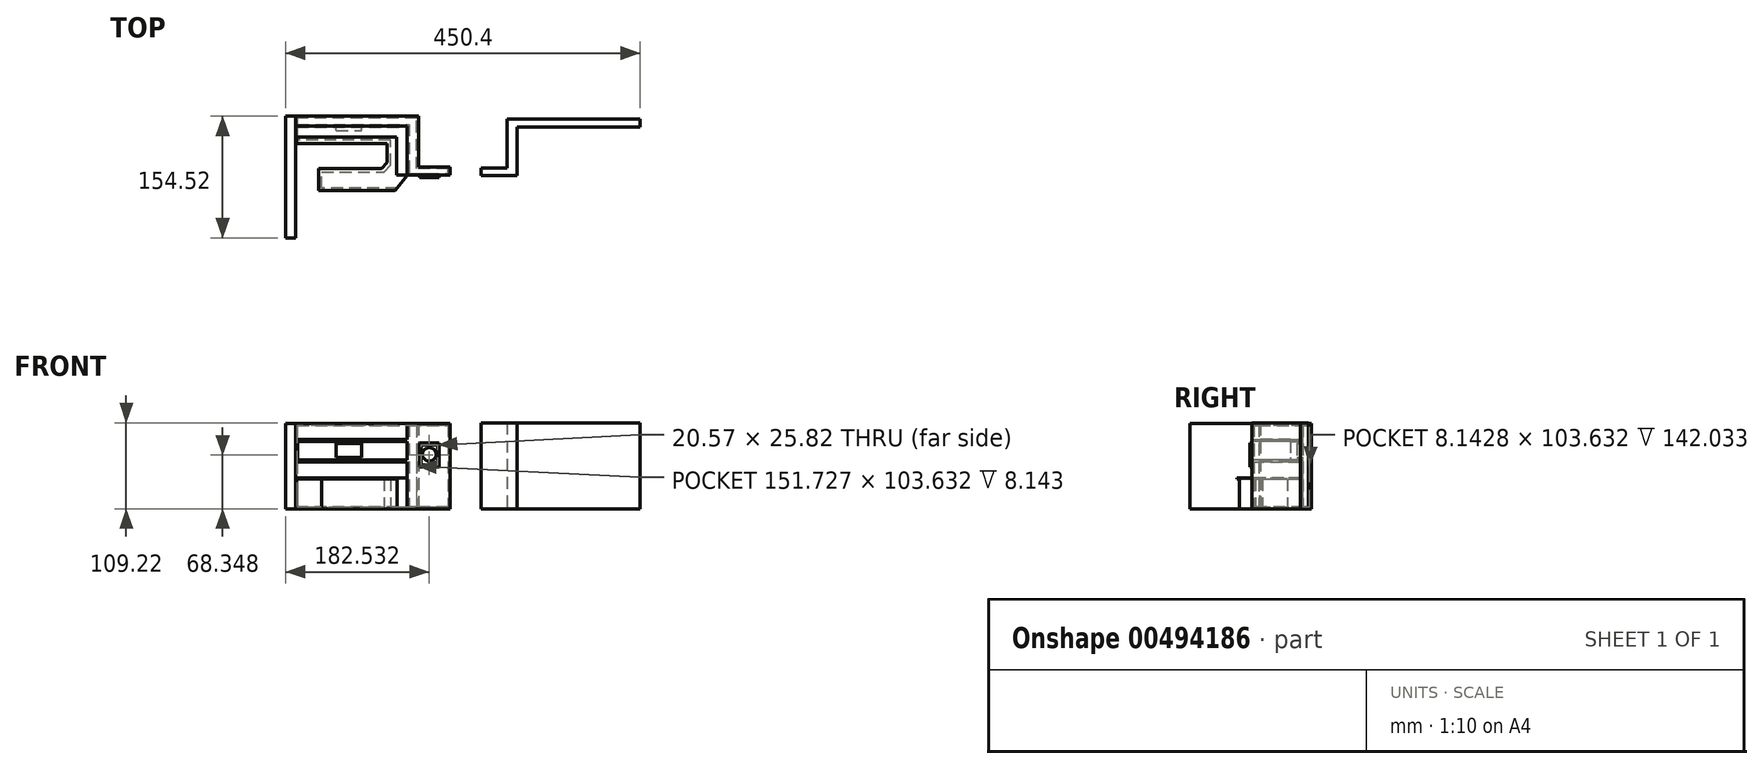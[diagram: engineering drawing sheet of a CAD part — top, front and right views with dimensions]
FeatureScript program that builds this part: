
annotation { "Feature Type Name" : "Feature", "Feature Type Description" : "" }
export const myFeature = defineFeature(function(context is Context, id is Id, definition is map)
    precondition{}
    {
        {
            var Q0;
            Q0=qCreatedBy(makeId("Top.planeOp"),FACE);
            var sketch = newSketch(context, id + "F0", { "sketchPlane" : qUnion([Q0])});
            skLineSegment(sketch, "E0", {"start": v(-74.74, 33.18) * mm, "end": v(67.3, 33.18) * mm});
            skLineSegment(sketch, "E1", {"start": v(67.3, 33.18) * mm, "end": v(67.3, -29.15) * mm});
            skLineSegment(sketch, "E2", {"start": v(67.3, -29.15) * mm, "end": v(121.57, -29.15) * mm});
            skLineSegment(sketch, "E3", {"start": v(121.57, -29.15) * mm, "end": v(121.57, -18.6) * mm});
            skLineSegment(sketch, "E4", {"start": v(121.57, -18.6) * mm, "end": v(81.56, -18.6) * mm});
            skLineSegment(sketch, "E5", {"start": v(81.56, -18.6) * mm, "end": v(81.56, 45.9) * mm});
            skLineSegment(sketch, "E6", {"start": v(81.56, 45.9) * mm, "end": v(-74.74, 45.9) * mm});
            skLineSegment(sketch, "E7", {"start": v(-74.74, 45.9) * mm, "end": v(-74.74, 33.18) * mm});
            skSolve(sketch);
        }
        {
            var Q0;
            Q0 = qSketchRegion(id + "F0", true);
            extrude(context, id + "F1", {"entities" : qUnion([Q0]), "depth" : 108.2 * mm});
        }
        {
            var Q0;
            Q0=makeQuery(id+"F1.opExtrude","SWEPT_FACE",FACE,{"disambiguationData":[OSD([sQuery(id+"F0.wireOp",EDGE,"E2")])]});
            var sketch = newSketch(context, id + "F2", { "sketchPlane" : qUnion([Q0])});
            skLineSegment(sketch, "E8.bottom", {"start": v(82.72, 83.55) * mm, "end": v(107.86, 83.55) * mm});
            skLineSegment(sketch, "E8.top", {"start": v(82.72, 53.15) * mm, "end": v(107.86, 53.15) * mm});
            skLineSegment(sketch, "E8.left", {"start": v(82.72, 83.55) * mm, "end": v(82.72, 53.15) * mm});
            skLineSegment(sketch, "E8.right", {"start": v(107.86, 83.55) * mm, "end": v(107.86, 53.15) * mm});
            skSolve(sketch);
        }
        {
            var Q0;
            Q0=makeQuery(id+"F2.imprint","IMPRINT",FACE,{"disambiguationData":[TD([[makeQuery(id+"F2.imprint","IMPRINT",EDGE,{"derivedFrom":sQuery(id+"F2.wireOp",EDGE,"E8.bottom")}),-1.0]])]});
            extrude(context, id + "F3", {"entities" : qUnion([Q0]), "operationType" : NewBodyOperationType.ADD, "depth" : 2.8 * mm});
        }
        {
            var Q0;
            Q0=makeQuery(id+"F3.opExtrude","CAP_FACE",FACE,{"disambiguationData":[OSD([sQuery(id+"F2.wireOp",EDGE,"E8.bottom"),sQuery(id+"F2.wireOp",EDGE,"E8.top"),sQuery(id+"F2.wireOp",EDGE,"E8.left"),sQuery(id+"F2.wireOp",EDGE,"E8.right")])],"isStart":false});
            shell(context, id + "F4", {"entities" : qUnion([Q0]), "thickness" : 2.3 * mm});
        }
        {
            var Q0;
            Q0=makeQuery(id+"F1.opExtrude","SWEPT_FACE",FACE,{"disambiguationData":[OSD([sQuery(id+"F0.wireOp",EDGE,"E2")])]});
            var sketch = newSketch(context, id + "F5", { "sketchPlane" : qUnion([Q0])});
            skCircle(sketch, "E9", {"center": v(95.2, 69.05) * mm, "radius": 8.6 * mm});
            skSolve(sketch);
        }
        {
            var Q0;
            Q0 = qSketchRegion(id + "F5", true);
            extrude(context, id + "F6", {"entities" : qUnion([Q0]), "depth" : 2.3 * mm});
        }
        {
            var Q0;
            Q0=qCreatedBy(makeId("Top.planeOp"),FACE);
            var sketch = newSketch(context, id + "F7", { "sketchPlane" : qUnion([Q0])});
            skLineSegment(sketch, "E10", {"start": v(67.08, -29.3) * mm, "end": v(54.42, -45.59) * mm});
            skLineSegment(sketch, "E11", {"start": v(54.42, -45.59) * mm, "end": v(-41.46, -45.59) * mm});
            skLineSegment(sketch, "E12", {"start": v(-41.46, -45.59) * mm, "end": v(-41.46, -25.3) * mm});
            skLineSegment(sketch, "E13", {"start": v(-41.46, -25.3) * mm, "end": v(37.83, -25.3) * mm});
            skLineSegment(sketch, "E14", {"start": v(37.83, -25.3) * mm, "end": v(45.94, -16.45) * mm});
            skLineSegment(sketch, "E15", {"start": v(45.94, -16.45) * mm, "end": v(45.94, 15.26) * mm});
            skLineSegment(sketch, "E16", {"start": v(45.94, 15.26) * mm, "end": v(-73.18, 15.26) * mm});
            skLineSegment(sketch, "E17", {"start": v(-73.18, 15.26) * mm, "end": v(-73.18, 32.23) * mm});
            skLineSegment(sketch, "E18", {"start": v(-73.18, 32.23) * mm, "end": v(66.23, 32.23) * mm});
            skLineSegment(sketch, "E19", {"start": v(66.23, 32.23) * mm, "end": v(67.08, -29.3) * mm});
            skSolve(sketch);
        }
        {
            var Q0;
            Q0=makeQuery(id+"F7.imprint","IMPRINT",FACE,{"disambiguationData":[TD([[makeQuery(id+"F7.imprint","IMPRINT",EDGE,{"derivedFrom":sQuery(id+"F7.wireOp",EDGE,"E10")}),-1.0]])]});
            extrude(context, id + "F8", {"entities" : qUnion([Q0]), "depth" : 37.6 * mm});
        }
        {
            var Q0;
            Q0=makeQuery(id+"F8.opExtrude","CAP_FACE",FACE,{"disambiguationData":[OSD([sQuery(id+"F7.wireOp",EDGE,"E10"),sQuery(id+"F7.wireOp",EDGE,"E11"),sQuery(id+"F7.wireOp",EDGE,"E12"),sQuery(id+"F7.wireOp",EDGE,"E13"),sQuery(id+"F7.wireOp",EDGE,"E14"),sQuery(id+"F7.wireOp",EDGE,"E15"),sQuery(id+"F7.wireOp",EDGE,"E16"),sQuery(id+"F7.wireOp",EDGE,"E17"),sQuery(id+"F7.wireOp",EDGE,"E18"),sQuery(id+"F7.wireOp",EDGE,"E19")])],"isStart":false});
            var sketch = newSketch(context, id + "F9", { "sketchPlane" : qUnion([Q0])});
            skLineSegment(sketch, "E20", {"start": v(-73.18, 32.23) * mm, "end": v(-73.18, 10.85) * mm});
            skPoint(sketch, "E20.endSnap0", {"position": v(-73.18, 23.75) * mm});
            skLineSegment(sketch, "E21", {"start": v(-73.18, 10.85) * mm, "end": v(41.6, 10.85) * mm});
            skLineSegment(sketch, "E22", {"start": v(41.6, 10.85) * mm, "end": v(41.6, -13.34) * mm});
            skLineSegment(sketch, "E23", {"start": v(41.6, -13.34) * mm, "end": v(34.62, -20.48) * mm});
            skLineSegment(sketch, "E24", {"start": v(34.62, -20.48) * mm, "end": v(-45.22, -20.48) * mm});
            skLineSegment(sketch, "E25", {"start": v(-45.22, -20.48) * mm, "end": v(-45.22, -48.66) * mm});
            skLineSegment(sketch, "E26", {"start": v(-45.22, -48.66) * mm, "end": v(52.05, -48.66) * mm});
            skLineSegment(sketch, "E27", {"start": v(52.05, -48.66) * mm, "end": v(67.08, -29.3) * mm});
            skLineSegment(sketch, "E28", {"start": v(67.08, -29.3) * mm, "end": v(67.08, -29.3) * mm});
            skLineSegment(sketch, "E29", {"start": v(67.08, -29.3) * mm, "end": v(67.08, 33.1) * mm});
            skLineSegment(sketch, "E30", {"start": v(67.08, 33.1) * mm, "end": v(-73.18, 32.23) * mm});
            skSolve(sketch);
        }
        {
            var Q0;
            Q0 = qSketchRegion(id + "F9", true);
            extrude(context, id + "F10", {"entities" : qUnion([Q0]), "operationType" : NewBodyOperationType.ADD, "depth" : 1.78 * mm});
        }
        {
            var Q0;
            Q0=makeQuery(id+"F1.opExtrude","SWEPT_FACE",FACE,{"disambiguationData":[OSD([sQuery(id+"F0.wireOp",EDGE,"E0")])]});
            var sketch = newSketch(context, id + "F11", { "sketchPlane" : qUnion([Q0])});
            skLineSegment(sketch, "E31.bottom", {"start": v(-74.74, 59.33) * mm, "end": v(67.3, 59.33) * mm});
            skLineSegment(sketch, "E31.top", {"start": v(-74.74, 88.1) * mm, "end": v(67.3, 88.1) * mm});
            skLineSegment(sketch, "E31.left", {"start": v(-74.74, 59.33) * mm, "end": v(-74.74, 88.1) * mm});
            skLineSegment(sketch, "E31.right", {"start": v(67.3, 59.33) * mm, "end": v(67.3, 88.1) * mm});
            skSolve(sketch);
        }
        {
            var Q0;
            Q0 = qSketchRegion(id + "F11", true);
            extrude(context, id + "F12", {"entities" : qUnion([Q0]), "operationType" : NewBodyOperationType.ADD, "depth" : 13.97 * mm});
        }
        {
            var Q0;
            Q0=makeQuery(id+"F12.opExtrude","CAP_FACE",FACE,{"disambiguationData":[OSD([sQuery(id+"F11.wireOp",EDGE,"E31.bottom"),sQuery(id+"F11.wireOp",EDGE,"E31.top"),sQuery(id+"F11.wireOp",EDGE,"E31.left"),sQuery(id+"F11.wireOp",EDGE,"E31.right")])],"isStart":false});
            shell(context, id + "F13", {"entities" : qUnion([Q0]), "thickness" : 2.54 * mm});
        }
        {
            var Q0;
            Q0=makeQuery(id+"F1.opExtrude","SWEPT_FACE",FACE,{"disambiguationData":[OSD([sQuery(id+"F0.wireOp",EDGE,"E1")])]});
            var sketch = newSketch(context, id + "F14", { "sketchPlane" : qUnion([Q0])});
            skLineSegment(sketch, "E32.bottom", {"start": v(-19.21, 88.1) * mm, "end": v(29.15, 88.1) * mm});
            skLineSegment(sketch, "E32.top", {"start": v(-19.21, 59.33) * mm, "end": v(29.15, 59.33) * mm});
            skLineSegment(sketch, "E32.left", {"start": v(-19.21, 88.1) * mm, "end": v(-19.21, 59.33) * mm});
            skLineSegment(sketch, "E32.right", {"start": v(29.15, 88.1) * mm, "end": v(29.15, 59.33) * mm});
            skSolve(sketch);
        }
        {
            var Q0;
            Q0 = qSketchRegion(id + "F14", true);
            extrude(context, id + "F15", {"entities" : qUnion([Q0]), "operationType" : NewBodyOperationType.ADD, "depth" : 13.46 * mm});
        }
        {
            var Q0;
            Q0=makeQuery(id+"F15.opExtrude","CAP_FACE",FACE,{"disambiguationData":[OSD([sQuery(id+"F14.wireOp",EDGE,"E32.bottom"),sQuery(id+"F14.wireOp",EDGE,"E32.top"),sQuery(id+"F14.wireOp",EDGE,"E32.left"),sQuery(id+"F14.wireOp",EDGE,"E32.right")])],"isStart":false});
            shell(context, id + "F16", {"entities" : qUnion([Q0]), "thickness" : 2.54 * mm});
        }
        {
            var Q0;
            Q0=makeQuery(id+"F16.opShell","OFFSET_FACE",FACE,{"disambiguationData":[OSD([sQuery(id+"F14.wireOp",EDGE,"E32.left")])]});
            extrude(context, id + "F17", {"entities" : qUnion([Q0]), "operationType" : NewBodyOperationType.REMOVE, "oppositeDirection" : true, "depth" : 3.05 * mm});
        }
        {
            var Q0;
            Q0=makeQuery(id+"F16.opShell","OFFSET_FACE",FACE,{"disambiguationData":[OSD([sQuery(id+"F0.wireOp",EDGE,"E2"),sQuery(id+"F14.wireOp",EDGE,"E32.right")])]});
            extrude(context, id + "F18", {"entities" : qUnion([Q0]), "operationType" : NewBodyOperationType.REMOVE, "oppositeDirection" : true, "depth" : 6.86 * mm});
        }
        {
            var Q0;
            Q0=makeQuery(id+"F13.opShell","OFFSET_FACE",FACE,{"disambiguationData":[OSD([sQuery(id+"F0.wireOp",EDGE,"E0")])]});
            var sketch = newSketch(context, id + "F19", { "sketchPlane" : qUnion([Q0])});
            skLineSegment(sketch, "E33.bottom", {"start": v(-22.93, 82.65) * mm, "end": v(9.06, 82.65) * mm});
            skLineSegment(sketch, "E33.top", {"start": v(-22.93, 65.22) * mm, "end": v(9.06, 65.22) * mm});
            skLineSegment(sketch, "E33.left", {"start": v(-22.93, 82.65) * mm, "end": v(-22.93, 65.22) * mm});
            skLineSegment(sketch, "E33.right", {"start": v(9.06, 82.65) * mm, "end": v(9.06, 65.22) * mm});
            skSolve(sketch);
        }
        {
            var Q0;
            Q0 = qSketchRegion(id + "F19", true);
            extrude(context, id + "F20", {"entities" : qUnion([Q0]), "operationType" : NewBodyOperationType.ADD, "depth" : 5.33 * mm});
        }
        {
            var Q0;
            Q0=qCreatedBy(makeId("Top.planeOp"),FACE);
            var sketch = newSketch(context, id + "F21", { "sketchPlane" : qUnion([Q0])});
            skLineSegment(sketch, "E34", {"start": v(160.88, -29.37) * mm, "end": v(160.88, -20.14) * mm});
            skLineSegment(sketch, "E35", {"start": v(160.88, -20.14) * mm, "end": v(194.31, -20.14) * mm});
            skLineSegment(sketch, "E36", {"start": v(194.31, -20.14) * mm, "end": v(194.31, 42.26) * mm});
            skLineSegment(sketch, "E37", {"start": v(194.31, 42.26) * mm, "end": v(363.16, 42.26) * mm});
            skLineSegment(sketch, "E38", {"start": v(363.16, 42.26) * mm, "end": v(363.16, 31.95) * mm});
            skLineSegment(sketch, "E39", {"start": v(363.16, 31.95) * mm, "end": v(206.8, 31.95) * mm});
            skLineSegment(sketch, "E40", {"start": v(206.8, 31.95) * mm, "end": v(206.8, -29.37) * mm});
            skLineSegment(sketch, "E41", {"start": v(206.8, -29.37) * mm, "end": v(160.88, -29.37) * mm});
            skSolve(sketch);
        }
        {
            var Q0;
            Q0 = qSketchRegion(id + "F21", true);
            extrude(context, id + "F22", {"entities" : qUnion([Q0]), "depth" : 109.22 * mm});
        }
        {
            var Q0;
            Q0=qCreatedBy(makeId("Top.planeOp"),FACE);
            var sketch = newSketch(context, id + "F23", { "sketchPlane" : qUnion([Q0])});
            skLineSegment(sketch, "E42.bottom", {"start": v(-74.87, 45.77) * mm, "end": v(-87.24, 45.77) * mm});
            skLineSegment(sketch, "E42.top", {"start": v(-74.87, -108.62) * mm, "end": v(-87.24, -108.62) * mm});
            skLineSegment(sketch, "E42.left", {"start": v(-74.87, 45.77) * mm, "end": v(-74.87, -108.62) * mm});
            skLineSegment(sketch, "E42.right", {"start": v(-87.24, 45.77) * mm, "end": v(-87.24, -108.62) * mm});
            skSolve(sketch);
        }
        {
            var Q0;
            Q0 = qSketchRegion(id + "F23", true);
            extrude(context, id + "F24", {"entities" : qUnion([Q0]), "depth" : 108.2 * mm});
        }
    });
